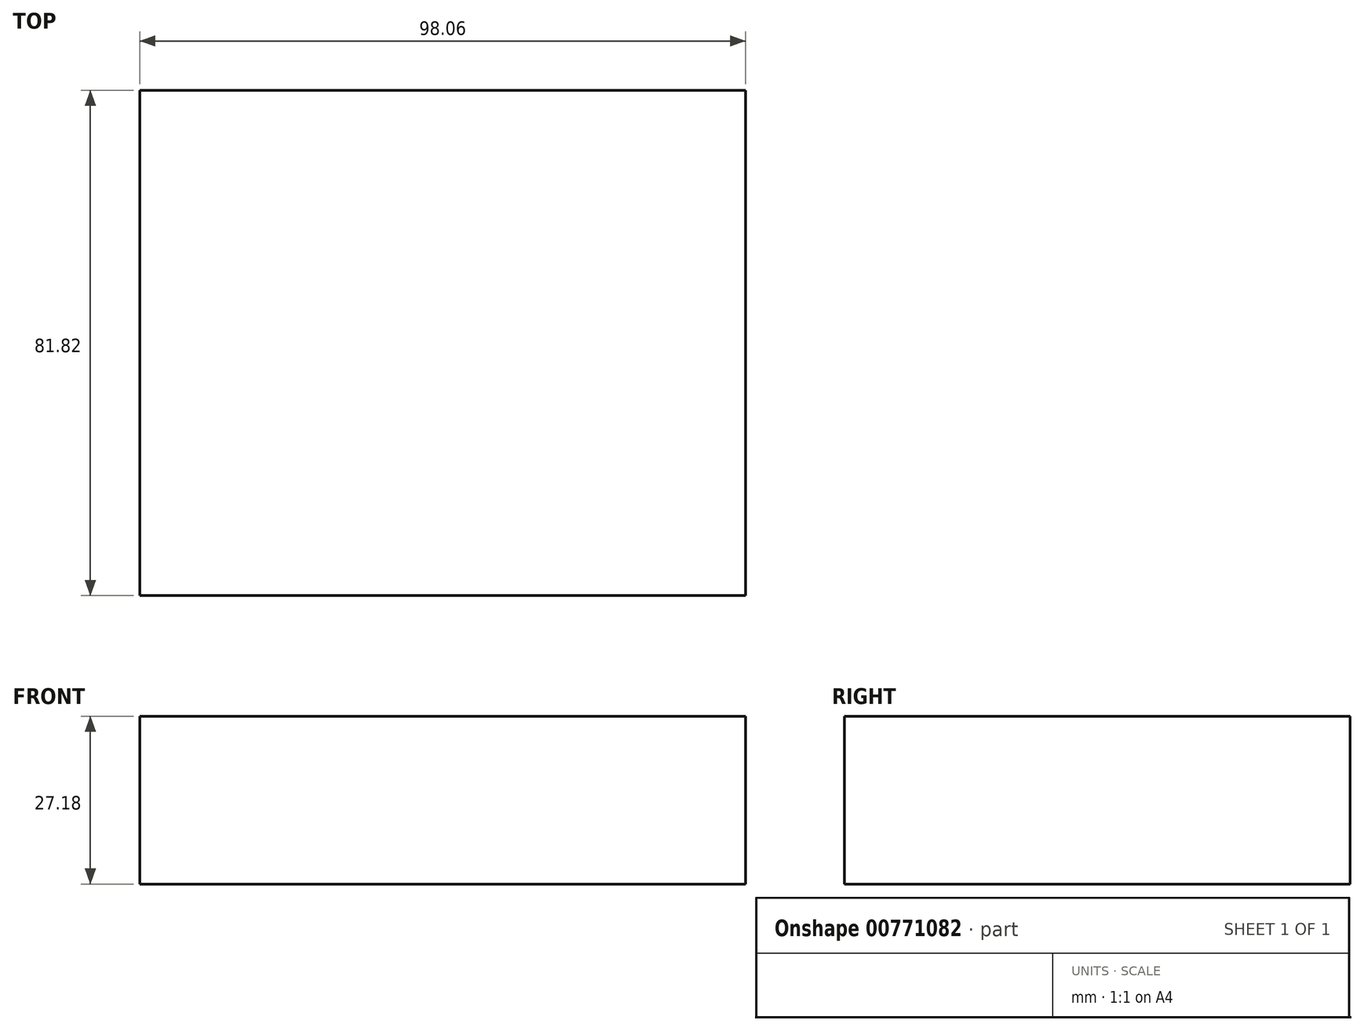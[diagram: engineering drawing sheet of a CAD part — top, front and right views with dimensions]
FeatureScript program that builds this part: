
annotation { "Feature Type Name" : "Feature", "Feature Type Description" : "" }
export const myFeature = defineFeature(function(context is Context, id is Id, definition is map)
    precondition{}
    {
        {
            var Q0;
            Q0=qCreatedBy(makeId("Top.planeOp"),FACE);
            var sketch = newSketch(context, id + "F0", { "sketchPlane" : qUnion([Q0])});
            skLineSegment(sketch, "E0.bottom", {"start": v(-45.57, -47.68) * mm, "end": v(52.49, -47.68) * mm});
            skLineSegment(sketch, "E0.top", {"start": v(-45.57, 34.14) * mm, "end": v(52.49, 34.14) * mm});
            skLineSegment(sketch, "E0.left", {"start": v(-45.57, -47.68) * mm, "end": v(-45.57, 34.14) * mm});
            skLineSegment(sketch, "E0.right", {"start": v(52.49, -47.68) * mm, "end": v(52.49, 34.14) * mm});
            skSolve(sketch);
        }
        {
            var Q0;
            Q0=makeQuery(id+"F0.imprint","IMPRINT",FACE,{"disambiguationData":[TD([[makeQuery(id+"F0.imprint","IMPRINT",EDGE,{"derivedFrom":sQuery(id+"F0.wireOp",EDGE,"E0.bottom")}),1.0]])]});
            extrude(context, id + "F1", {"entities" : qUnion([Q0]), "depth" : 27.18 * mm, "offsetDistance" : 25.4 * mm});
        }
        {
            var Q0;
            Q0=qCreatedBy(makeId("Top.planeOp"),FACE);
            var sketch = newSketch(context, id + "F2", { "sketchPlane" : qUnion([Q0])});
            skCircle(sketch, "E1", {"center": v(-16.3, 25.77) * mm, "radius": 22.55 * mm});
            skSolve(sketch);
        }
        {
            var Q0;
            Q0=sQuery(id+"F2.wireOp",EDGE,"E1");
            extrude(context, id + "F3", {"bodyType" : ToolBodyType.SURFACE, "surfaceEntities" : qUnion([Q0]), "depth" : 25.4 * mm, "offsetDistance" : 25.4 * mm});
        }
    });
